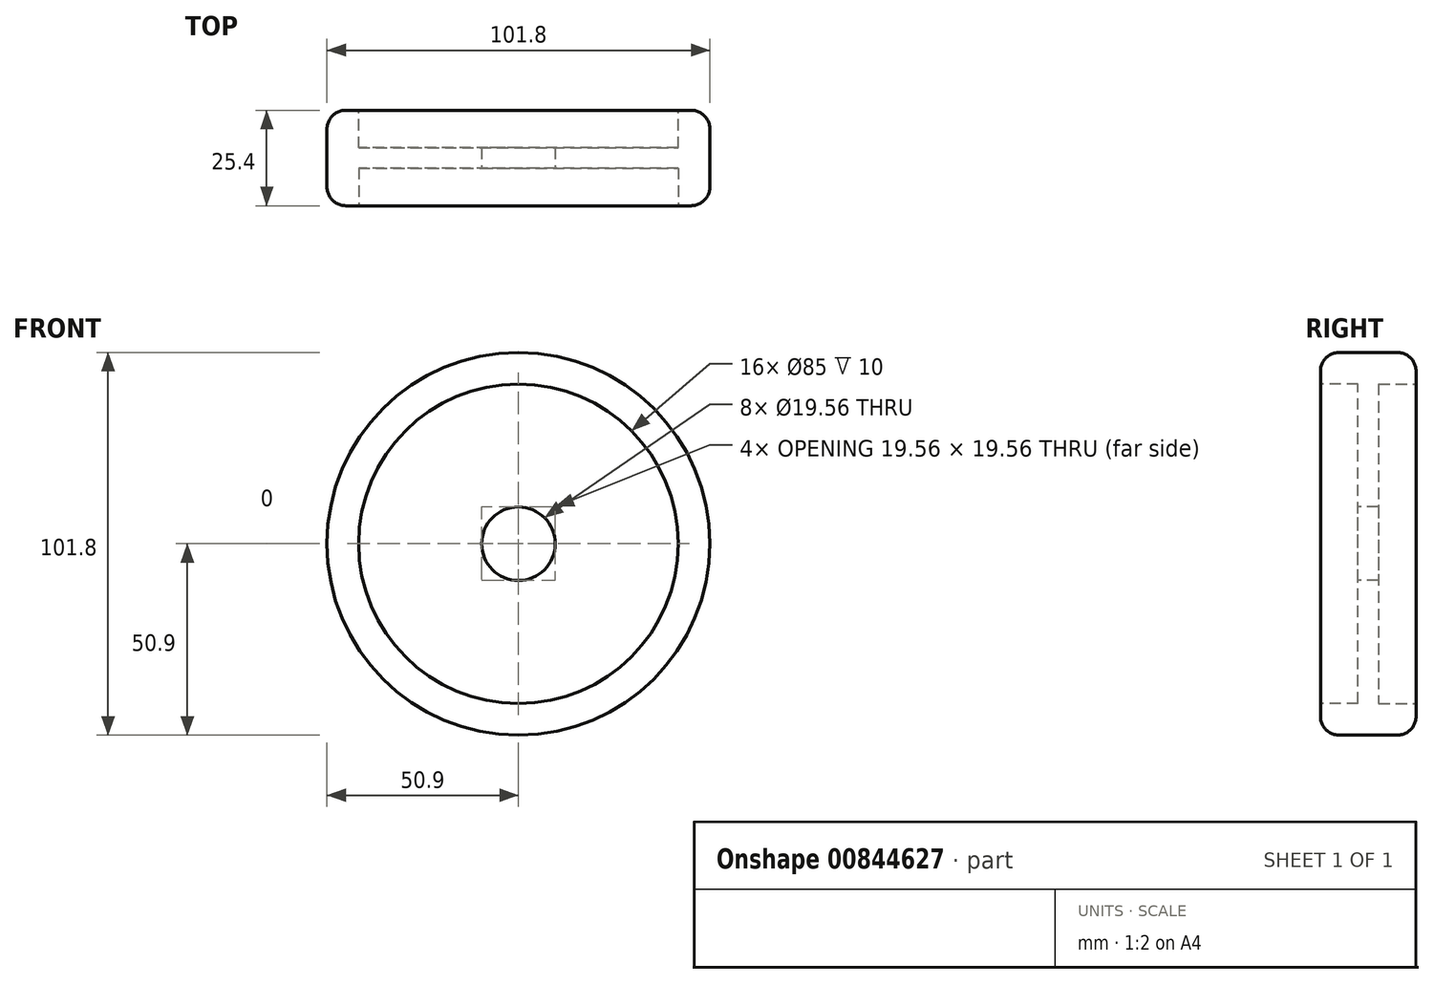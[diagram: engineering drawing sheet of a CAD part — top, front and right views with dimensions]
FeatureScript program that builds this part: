
annotation { "Feature Type Name" : "Feature", "Feature Type Description" : "" }
export const myFeature = defineFeature(function(context is Context, id is Id, definition is map)
    precondition{}
    {
        {
            var Q0;
            Q0=qCreatedBy(makeId("Front.planeOp"),FACE);
            var sketch = newSketch(context, id + "F0", { "sketchPlane" : qUnion([Q0])});
            skCircle(sketch, "E0", {"center": v(0, 0) * mm, "radius": 50.9 * mm});
            skCircle(sketch, "E1.0", {"center": v(0, 0) * mm, "radius": 40.9 * mm});
            skSolve(sketch);
        }
        {
            var Q0;
            Q0=makeQuery(id+"F0.imprint","IMPRINT",FACE,{"disambiguationData":[TD([[makeQuery(id+"F0.imprint","IMPRINT",EDGE,{"derivedFrom":sQuery(id+"F0.wireOp",EDGE,"E1.0")}),1.0]])]});
            var Q1;
            Q1=makeQuery(id+"F0.imprint","IMPRINT",FACE,{"disambiguationData":[TD([[makeQuery(id+"F0.imprint","IMPRINT",EDGE,{"derivedFrom":sQuery(id+"F0.wireOp",EDGE,"E0")}),1.0]])]});
            extrude(context, id + "F1", {"entities" : qUnion([Q0, Q1]), "depth" : 25.4 * mm, "offsetDistance" : 25 * mm, "symmetric" : true});
        }
        {
            var Q0;
            Q0=makeQuery(id+"F1.opExtrude","CAP_EDGE",EDGE,{"disambiguationData":[OSD([sQuery(id+"F0.wireOp",EDGE,"E0")])],"isStart":false});
            var Q1;
            Q1=makeQuery(id+"F1.opExtrude","CAP_EDGE",EDGE,{"disambiguationData":[OSD([sQuery(id+"F0.wireOp",EDGE,"E0")])],"isStart":true});
            fillet(context, id + "F2", {"entities" : qUnion([Q0, Q1]), "radius" : 5 * mm, "tangentPropagation" : true, "allowEdgeOverflow" : false});
        }
        {
            var Q0;
            Q0=makeQuery(id+"F1.opExtrude","CAP_FACE",FACE,{"disambiguationData":[OSD([sQuery(id+"F0.wireOp",EDGE,"E0")])],"isStart":false});
            var sketch = newSketch(context, id + "F3", { "sketchPlane" : qUnion([Q0])});
            skCircle(sketch, "E2", {"center": v(0, 0) * mm, "radius": 42.5 * mm});
            skSolve(sketch);
        }
        {
            var Q0;
            Q0=makeQuery(id+"F3.imprint","IMPRINT",FACE,{"disambiguationData":[TD([[makeQuery(id+"F3.imprint","IMPRINT",EDGE,{"derivedFrom":sQuery(id+"F3.wireOp",EDGE,"E2")}),1.0]])]});
            extrude(context, id + "F4", {"entities" : qUnion([Q0]), "operationType" : NewBodyOperationType.REMOVE, "oppositeDirection" : true, "depth" : 10 * mm, "offsetDistance" : 25 * mm});
        }
        {
            var Q0;
            Q0=makeQuery(id+"F1.opExtrude","CAP_FACE",FACE,{"disambiguationData":[OSD([sQuery(id+"F0.wireOp",EDGE,"E0")])],"isStart":true});
            var sketch = newSketch(context, id + "F5", { "sketchPlane" : qUnion([Q0])});
            skCircle(sketch, "E3", {"center": v(0, 0) * mm, "radius": 42.5 * mm});
            skSolve(sketch);
        }
        {
            var Q0;
            Q0=makeQuery(id+"F5.imprint","IMPRINT",FACE,{"disambiguationData":[TD([[makeQuery(id+"F5.imprint","IMPRINT",EDGE,{"derivedFrom":sQuery(id+"F5.wireOp",EDGE,"E3")}),1.0]])]});
            extrude(context, id + "F6", {"entities" : qUnion([Q0]), "operationType" : NewBodyOperationType.REMOVE, "oppositeDirection" : true, "depth" : 10 * mm, "offsetDistance" : 25 * mm});
        }
        {
            var Q0;
            Q0=makeQuery(id+"F4.boolean.opBoolean","COPY",FACE,{"derivedFrom":makeQuery(id+"F4.opExtrude","CAP_FACE",FACE,{"disambiguationData":[OSD([sQuery(id+"F3.wireOp",EDGE,"E2")])],"isStart":false})});
            var sketch = newSketch(context, id + "F7", { "sketchPlane" : qUnion([Q0])});
            skCircle(sketch, "E4", {"center": v(0, 0) * mm, "radius": 9.78 * mm});
            skSolve(sketch);
        }
        {
            var Q0;
            Q0=makeQuery(id+"F7.imprint","IMPRINT",FACE,{"disambiguationData":[TD([[makeQuery(id+"F7.imprint","IMPRINT",EDGE,{"derivedFrom":sQuery(id+"F7.wireOp",EDGE,"E4")}),1.0]])]});
            extrude(context, id + "F8", {"entities" : qUnion([Q0]), "operationType" : NewBodyOperationType.REMOVE, "endBound" : BoundingType.UP_TO_NEXT, "oppositeDirection" : true, "depth" : 25 * mm, "offsetDistance" : 25 * mm});
        }
    });
